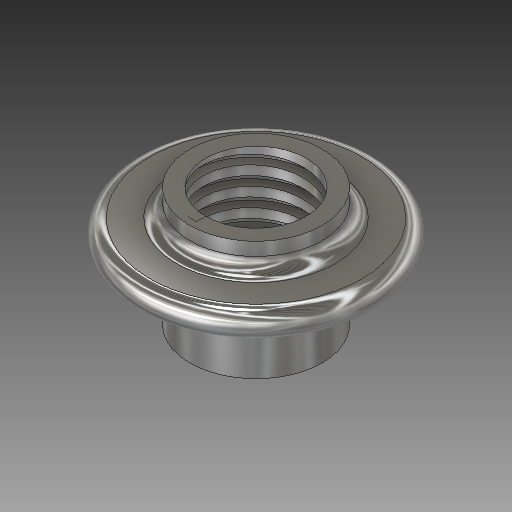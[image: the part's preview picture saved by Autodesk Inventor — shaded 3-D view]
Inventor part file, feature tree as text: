
AUTODESK INVENTOR PART (.ipt)
format: ipt  version: 2018 (Build 220112000, 112)  size: 346,112 bytes
history: native  units: in
note: dims shown in document units (in); Inventor stores cm internally (conversion verified against a paired STEP export)
features: sketch x2, revolve x1, helix x1
ambient origin geometry x8: Origin, YZ Plane, XZ Plane, XY Plane, X Axis, Y Axis, Z Axis, Center Point
bodies: Solid1 (feature_tree)
feature tree (4):
  revolve  "Revolution1"  [1 undecoded]
  helix  "Coil1"  [1 undecoded]
  sketch  "Sketch1"  dims[d7=90.0deg d15=0.1378in]
  sketch  "Sketch2"  dims[d16=0.2756in d17=2.2047in d18=0.3937in d19=0.0in d20=90.0deg d21=90.0deg d22=0.0in d23=0.0in]
note: 2 required parameter values undecoded (feature->parameter linkage not recoverable at this tier; creation-order binding heuristic only, values carry confidence <= 0.55)